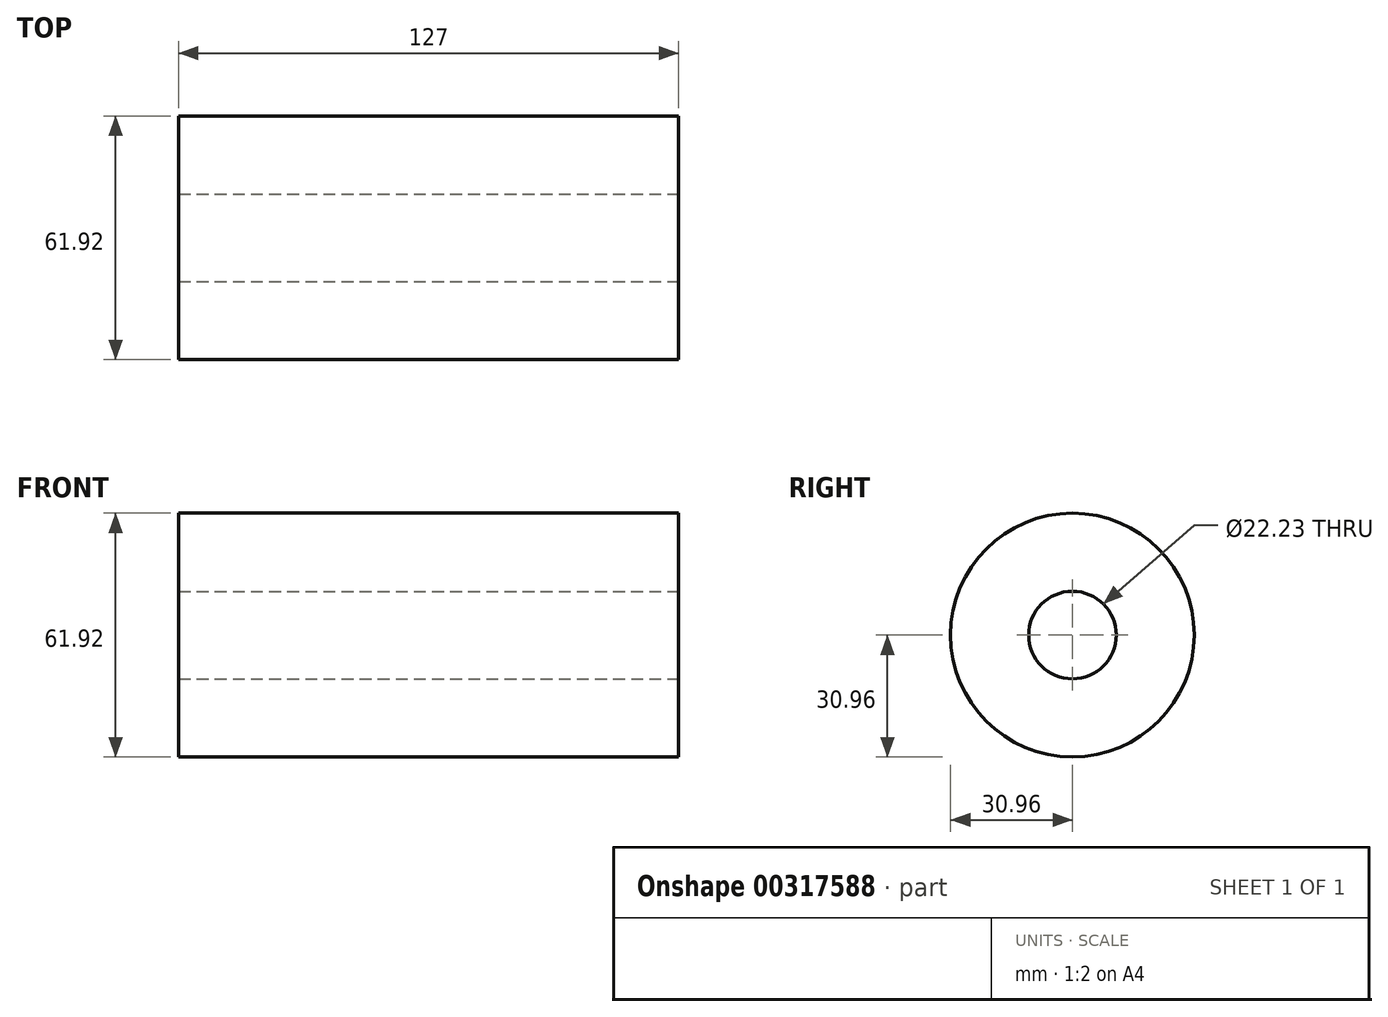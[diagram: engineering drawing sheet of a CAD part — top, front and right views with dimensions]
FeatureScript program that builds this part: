
annotation { "Feature Type Name" : "Feature", "Feature Type Description" : "" }
export const myFeature = defineFeature(function(context is Context, id is Id, definition is map)
    precondition{}
    {
        {
            var Q0;
            Q0=qCreatedBy(makeId("Right.planeOp"),FACE);
            var sketch = newSketch(context, id + "F0", { "sketchPlane" : qUnion([Q0])});
            skCircle(sketch, "E0", {"center": v(0, 0) * mm, "radius": 30.96 * mm});
            skSolve(sketch);
        }
        {
            var Q0;
            Q0=makeQuery(id+"F0.imprint","IMPRINT",FACE,{"disambiguationData":[TD([[makeQuery(id+"F0.imprint","IMPRINT",EDGE,{"derivedFrom":sQuery(id+"F0.wireOp",EDGE,"E0")}),1.0]])]});
            extrude(context, id + "F1", {"entities" : qUnion([Q0]), "endBound" : BoundingType.SYMMETRIC, "depth" : 127 * mm});
        }
        {
            var Q0;
            Q0=makeQuery(id+"F1.opExtrude","CAP_FACE",FACE,{"disambiguationData":[OSD([sQuery(id+"F0.wireOp",EDGE,"E0")])],"isStart":false});
            var sketch = newSketch(context, id + "F2", { "sketchPlane" : qUnion([Q0])});
            skCircle(sketch, "E1", {"center": v(0, 0) * mm, "radius": 11.11 * mm});
            skSolve(sketch);
        }
        {
            var Q0;
            Q0=sQuery(id+"F2.wireOp",VERTEX,"E1.center");
            var Q1;
            Q1=makeQuery(id+"F1.opExtrude","SWEPT_BODY",BODY,{"disambiguationData":[OSD([sQuery(id+"F0.wireOp",EDGE,"E0")])]});
            hole(context, id + "F3", {"style" : HoleStyle.SIMPLE, "endStyle" : HoleEndStyle.BLIND, "holeDiameter" : 22.22 * mm, "holeDepth" : 127 * mm, "tappedDepth" : 12.7 * mm, "tapClearance" : 3, "locations" : qUnion([Q0]), "scope" : qUnion([Q1])});
        }
    });
